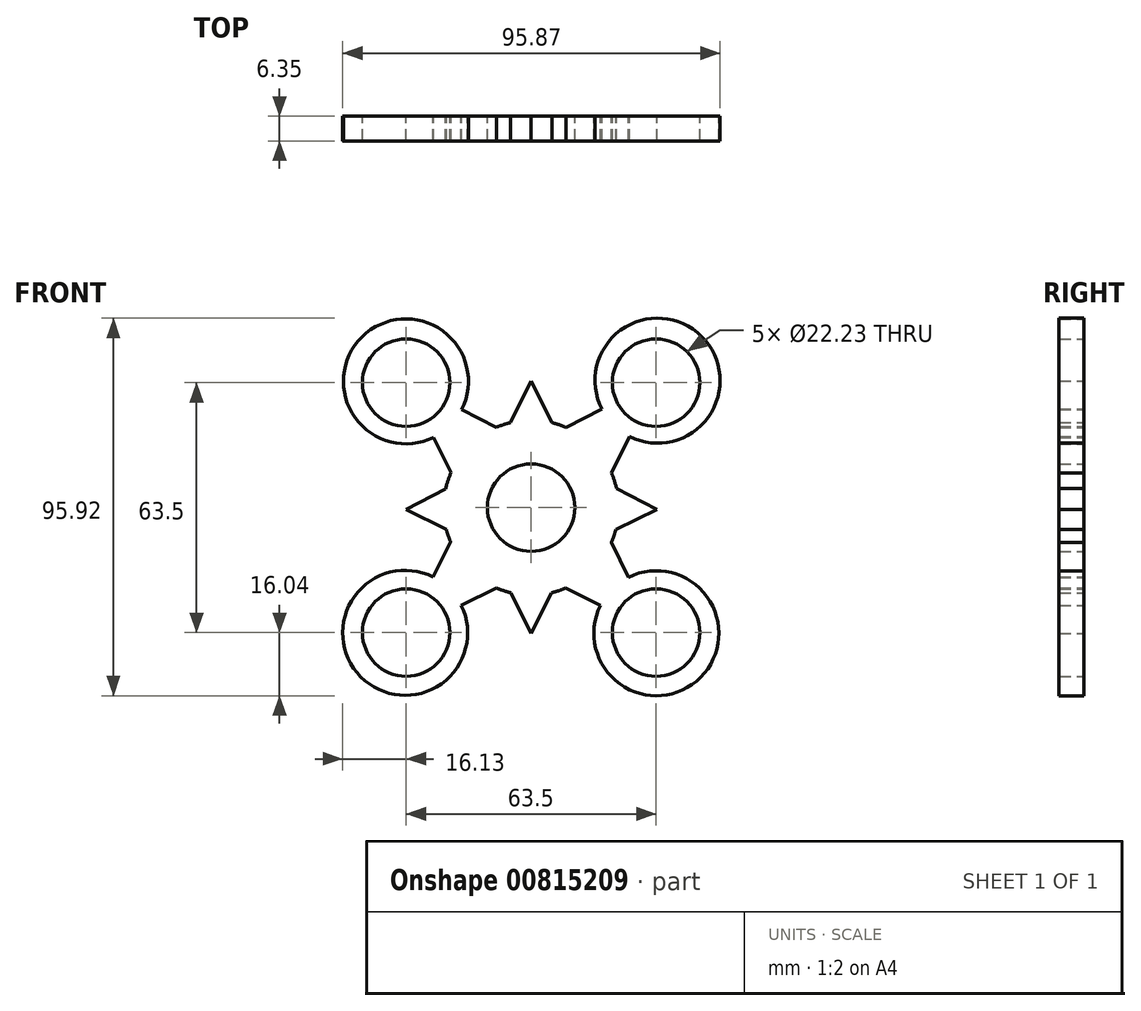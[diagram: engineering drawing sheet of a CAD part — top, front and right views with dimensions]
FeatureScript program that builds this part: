
annotation { "Feature Type Name" : "Feature", "Feature Type Description" : "" }
export const myFeature = defineFeature(function(context is Context, id is Id, definition is map)
    precondition{}
    {
        {
            var Q0;
            Q0=qCreatedBy(makeId("Front.planeOp"),FACE);
            var sketch = newSketch(context, id + "F0", { "sketchPlane" : qUnion([Q0])});
            skCircle(sketch, "E0", {"center": v(0, 0) * mm, "radius": 22.23 * mm});
            skCircle(sketch, "E1", {"center": v(32.12, 32.26) * mm, "radius": 15.88 * mm});
            skCircle(sketch, "E2", {"center": v(-31.8, 32.1) * mm, "radius": 15.88 * mm});
            skCircle(sketch, "E3", {"center": v(-32, -31.82) * mm, "radius": 15.88 * mm});
            skCircle(sketch, "E4", {"center": v(31.82, -31.91) * mm, "radius": 15.88 * mm});
            skPoint(sketch, "E5.8.internal.snap0", {"position": v(32.03, 15.92) * mm});
            skLineSegment(sketch, "E6", {"start": v(32.12, 32.26) * mm, "end": v(-32, -31.82) * mm});
            skLineSegment(sketch, "E7", {"start": v(-31.8, 32.1) * mm, "end": v(31.82, -31.91) * mm});
            skLineSegment(sketch, "E8", {"start": v(-31.8, 32.1) * mm, "end": v(0, -31.91) * mm});
            skLineSegment(sketch, "E9", {"start": v(0, -31.91) * mm, "end": v(32.12, 32.26) * mm});
            skLineSegment(sketch, "E10", {"start": v(-32, -31.82) * mm, "end": v(0, 32.18) * mm});
            skLineSegment(sketch, "E11", {"start": v(0, 32.18) * mm, "end": v(31.82, -31.91) * mm});
            skLineSegment(sketch, "E12", {"start": v(-31.8, 32.1) * mm, "end": v(31.95, -0.41) * mm});
            skLineSegment(sketch, "E13", {"start": v(32.12, 32.26) * mm, "end": v(-31.8, -0.41) * mm});
            skLineSegment(sketch, "E14", {"start": v(-32, -31.82) * mm, "end": v(31.95, -0.41) * mm});
            skLineSegment(sketch, "E15", {"start": v(31.82, -31.91) * mm, "end": v(-31.8, -0.41) * mm});
            skSolve(sketch);
        }
        {
            var Q0;
            Q0 = qSketchRegion(id + "F0", true);
            extrude(context, id + "F1", {"entities" : qUnion([Q0]), "depth" : 6.35 * mm, "offsetDistance" : 25.4 * mm});
        }
        {
            var Q0;
            Q0=qCreatedBy(makeId("Front.planeOp"),FACE);
            var sketch = newSketch(context, id + "F2", { "sketchPlane" : qUnion([Q0])});
            skCircle(sketch, "E16", {"center": v(-31.75, 31.75) * mm, "radius": 11.11 * mm});
            skCircle(sketch, "E17", {"center": v(31.75, 31.75) * mm, "radius": 11.11 * mm});
            skCircle(sketch, "E18", {"center": v(31.75, -31.75) * mm, "radius": 11.11 * mm});
            skCircle(sketch, "E19", {"center": v(-31.75, -31.75) * mm, "radius": 11.11 * mm});
            skCircle(sketch, "E20", {"center": v(0, 0) * mm, "radius": 11.11 * mm});
            skSolve(sketch);
        }
        {
            var Q0;
            Q0 = qSketchRegion(id + "F2", true);
            extrude(context, id + "F3", {"entities" : qUnion([Q0]), "operationType" : NewBodyOperationType.REMOVE, "endBound" : BoundingType.THROUGH_ALL, "depth" : 25.4 * mm, "offsetDistance" : 25.4 * mm});
        }
        {
            var Q0;
            Q0=qCreatedBy(makeId("Front.planeOp"),FACE);
            var sketch = newSketch(context, id + "F4", { "sketchPlane" : qUnion([Q0])});
            skCircle(sketch, "E21", {"center": v(0, 0) * mm, "radius": 21.59 * mm});
            skSolve(sketch);
        }
        {
            var Q0;
            Q0 = qSketchRegion(id + "F4", true);
            extrude(context, id + "F5", {"entities" : qUnion([Q0]), "operationType" : NewBodyOperationType.ADD, "depth" : 6.35 * mm, "offsetDistance" : 25.4 * mm});
        }
        {
            var Q0;
            Q0=qCreatedBy(makeId("Front.planeOp"),FACE);
            var sketch = newSketch(context, id + "F6", { "sketchPlane" : qUnion([Q0])});
            skCircle(sketch, "E22", {"center": v(0, 0) * mm, "radius": 11.11 * mm});
            skSolve(sketch);
        }
        {
            var Q0;
            Q0 = qSketchRegion(id + "F6", true);
            extrude(context, id + "F7", {"entities" : qUnion([Q0]), "operationType" : NewBodyOperationType.REMOVE, "endBound" : BoundingType.THROUGH_ALL, "depth" : 25.4 * mm, "offsetDistance" : 25.4 * mm});
        }
    });
